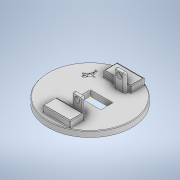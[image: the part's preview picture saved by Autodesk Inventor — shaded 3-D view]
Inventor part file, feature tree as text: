
AUTODESK INVENTOR PART (.ipt)
format: ipt  version: 2021 (Build 250183000, 183)  size: 522,240 bytes
history: native  units: mm
features: sketch x26, extrude x17, fillet x8, chamfer x6, other x1
ambient origin geometry x8: Origin, YZ Plane, XZ Plane, XY Plane, X Axis, Y Axis, Z Axis, Center Point
bodies: Body1 (feature_tree)
feature tree (58):
  other  "Sólido1"
  extrude  "Extrusión1"  Depth=10.0mm TaperAngle=0.0deg
  sketch  "Boceto2"  dims[d13=39.0mm d31=1.0mm d32=0.0mm]
  sketch  "Boceto3"  dims[d33=1.0mm d34=2.0mm d35=45.0deg d64=10.0mm d65=0.0mm d69=0.5mm d70=0.0mm]
  extrude  "Extrusión2"  Depth=1.0mm TaperAngle=0.0deg
  extrude  "Extrusión5"  Depth=10.0mm TaperAngle=0.0deg
  chamfer  "Chaflán1"  Distance=0.5mm
  sketch  "Boceto9"  dims[d79=1.6mm d80=45.4mm d81=1.6mm]
  sketch  "Boceto10"  dims[d82=12.0mm d83=0.5mm d84=0.0mm]
  sketch  "Boceto11"  dims[d85=1.0mm d92=10.5mm d93=0.0mm d94=30.0mm d95=0.0mm]
  extrude  "Extrusión6"  Depth=1.0mm TaperAngle=15.0deg
  extrude  "Extrusión7"  Depth=45.4mm
  fillet  "Empalme6"  Radius=1.6mm
  chamfer  "Chaflán2"  Distance=0.5mm
  sketch  "Boceto13"  dims[d99=12.75mm d100=8.0mm]
  extrude  "Extrusión8"  Depth=1.0mm TaperAngle=0.0deg
  fillet  "Empalme7"  Radius=30.0mm
  extrude  "Extrusión9"  Depth=10.0mm
  extrude  "Extrusión10"  Depth=8.0mm
  extrude  "Extrusión11"  Depth=10.0mm TaperAngle=0.0deg
  sketch  "Boceto18"  dims[d117=1.0mm d118=2.0mm d119=30.0deg]
  sketch  "Boceto19"  dims[d120=1.0mm d121=2.0mm d122=30.0deg d123=1.0mm d124=1.0mm]
  sketch  "Boceto20"  dims[d125=1.0mm]
  extrude  "Extrusión12"  Depth=900.0mm TaperAngle=0.0deg
  sketch  "Boceto22"  dims[d135=15.0mm]
  extrude  "Extrusión13"  Depth=4.0mm
  extrude  "Extrusión14"  Depth=1.0mm TaperAngle=30.0deg
  fillet  "Empalme8"  Radius=1.0mm
  fillet  "Empalme9"  Radius=1.0mm
  chamfer  "Chaflán3"  Distance=40.0mm Angle=360.0deg
  chamfer  "Chaflán4"  Distance=0.5mm
  chamfer  "Chaflán5"  [1 undecoded]
  chamfer  "Chaflán6"  Distance=0.5mm
  fillet  "Empalme10"  [1 undecoded]
  fillet  "Empalme11"  Radius=0.2mm
  fillet  "Empalme12"  Radius=44.5mm
  fillet  "Empalme13"  Radius=7.4mm
  sketch  "Boceto24"  dims[d167=0.5mm]
  extrude  "Extrusión15"  Depth=0.5mm TaperAngle=360.0deg
  extrude  "Extrusión16"  Depth=4.0mm TaperAngle=0.0deg
  sketch  "Boceto27"  dims[d170=10.5mm]
  extrude  "Extrusión17"  Depth=0.5mm
  extrude  "Extrusión18"  Depth=0.5mm
  extrude  "Extrusión19"  Depth=0.5mm
  sketch  "Boceto1"  dims[d1=10.0mm d2=0.0mm d11=20.0mm d12=0.0mm]
  sketch  "Boceto4"  dims[d71=1.0mm d72=1.0mm d73=2.0mm d74=15.0deg]
  sketch  "Boceto12"  dims[d96=10.0mm d97=0.0mm d98=10.0mm]
  sketch  "Boceto14"  dims[d101=6.4mm d102=10.0mm d103=0.0mm]
  sketch  "Boceto15"  dims[d105=19.5mm d106=0.0mm d107=900.0mm d108=0.0mm]
  sketch  "Boceto16"  dims[d109=4.0mm d110=4.0mm]
  sketch  "Boceto17"  dims[d111=1.0mm d112=2.0mm d113=30.0deg d114=1.0mm d115=2.0mm d116=30.0deg]
  sketch  "Boceto21"  dims[d126=1.0mm]
  sketch  "Boceto23"  dims[d144=7.0mm d145=7.0mm d146=7.0mm d147=7.0mm d148=7.0mm d149=7.0mm d150=7.0mm d151=7.0mm d153=40.0mm d155=360.0deg d157=2.3mm d158=0.5mm d162=0.5mm]
  sketch  "Boceto25"  dims[d168=0.0mm]
  sketch  "Boceto26"  dims[d169=10.0mm]
  sketch  "Boceto28"  dims[d171=7.0mm]
  sketch  "Boceto29"  dims[d172=7.5mm]
  sketch  "Boceto30"  dims[d173=0.5mm d174=0.0mm d176=0.5mm d177=0.0mm d178=0.2mm d179=0.0mm d180=44.5mm d181=7.4mm d182=40.0mm d184=360.0deg d186=4.0mm d187=0.0mm d59=0.5mm d60=0.872665mm d61=0.5mm d62=0.872665mm d104=0.872665mm]
note: 2 required parameter values undecoded (feature->parameter linkage not recoverable at this tier; creation-order binding heuristic only, values carry confidence <= 0.55)
